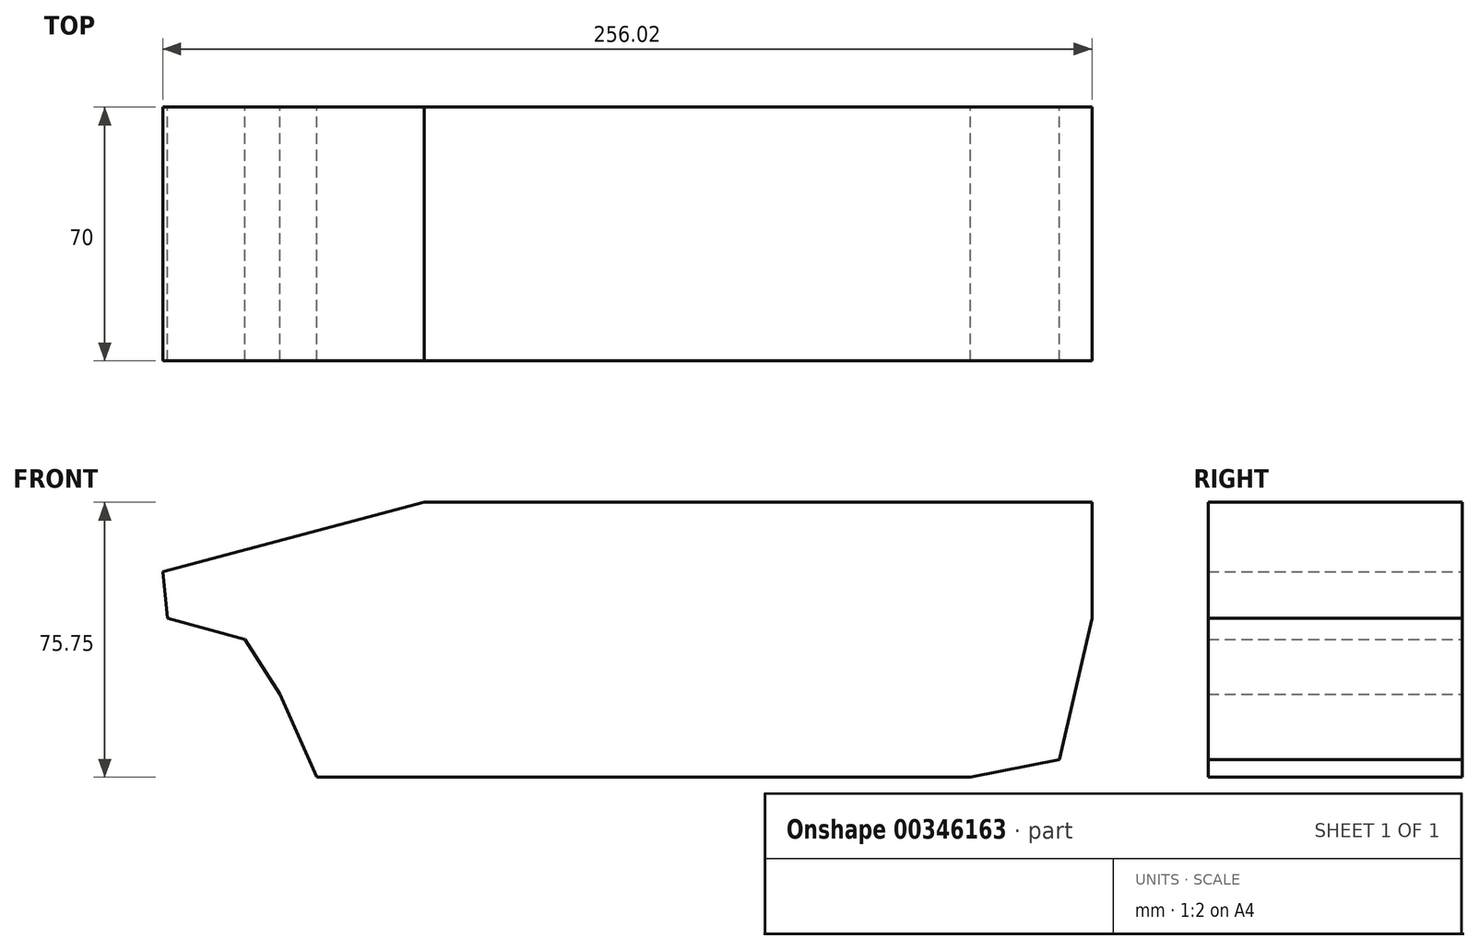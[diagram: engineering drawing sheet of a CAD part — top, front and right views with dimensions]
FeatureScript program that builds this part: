
annotation { "Feature Type Name" : "Feature", "Feature Type Description" : "" }
export const myFeature = defineFeature(function(context is Context, id is Id, definition is map)
    precondition{}
    {
        {
            var Q0;
            Q0=qCreatedBy(makeId("Front.planeOp"),FACE);
            var sketch = newSketch(context, id + "F0", { "sketchPlane" : qUnion([Q0])});
            skLineSegment(sketch, "E0", {"start": v(-43.21, 39.62) * mm, "end": v(140.79, 39.62) * mm});
            skLineSegment(sketch, "E1", {"start": v(140.79, 39.62) * mm, "end": v(140.79, 7.62) * mm});
            skLineSegment(sketch, "E2", {"start": v(140.79, 7.62) * mm, "end": v(131.8, -31.36) * mm});
            skLineSegment(sketch, "E3", {"start": v(131.8, -31.36) * mm, "end": v(107.25, -36.13) * mm});
            skLineSegment(sketch, "E4", {"start": v(107.25, -36.13) * mm, "end": v(-72.75, -36.13) * mm});
            skLineSegment(sketch, "E5", {"start": v(-72.75, -36.13) * mm, "end": v(-82.92, -13.29) * mm});
            skLineSegment(sketch, "E6", {"start": v(-82.92, -13.29) * mm, "end": v(-92.64, 1.86) * mm});
            skLineSegment(sketch, "E7", {"start": v(-92.64, 1.86) * mm, "end": v(-113.87, 7.63) * mm});
            skLineSegment(sketch, "E8", {"start": v(-113.87, 7.63) * mm, "end": v(-115.23, 20.56) * mm});
            skLineSegment(sketch, "E9", {"start": v(-115.23, 20.56) * mm, "end": v(-43.21, 39.62) * mm});
            skLineSegment(sketch, "E10", {"start": v(-113.87, 7.63) * mm, "end": v(140.79, 7.62) * mm});
            skSolve(sketch);
        }
        {
            var Q0;
            Q0=makeQuery(id+"F0.imprint","IMPRINT",FACE,{"disambiguationData":[TD([[makeQuery(id+"F0.imprint","IMPRINT",EDGE,{"derivedFrom":sQuery(id+"F0.wireOp",EDGE,"E0")}),-1.0]])]});
            var Q1;
            Q1=makeQuery(id+"F0.imprint","IMPRINT",FACE,{"disambiguationData":[TD([[makeQuery(id+"F0.imprint","IMPRINT",EDGE,{"derivedFrom":sQuery(id+"F0.wireOp",EDGE,"E2")}),-1.0]])]});
            extrude(context, id + "F1", {"entities" : qUnion([Q0, Q1]), "depth" : 70 * mm});
        }
    });
